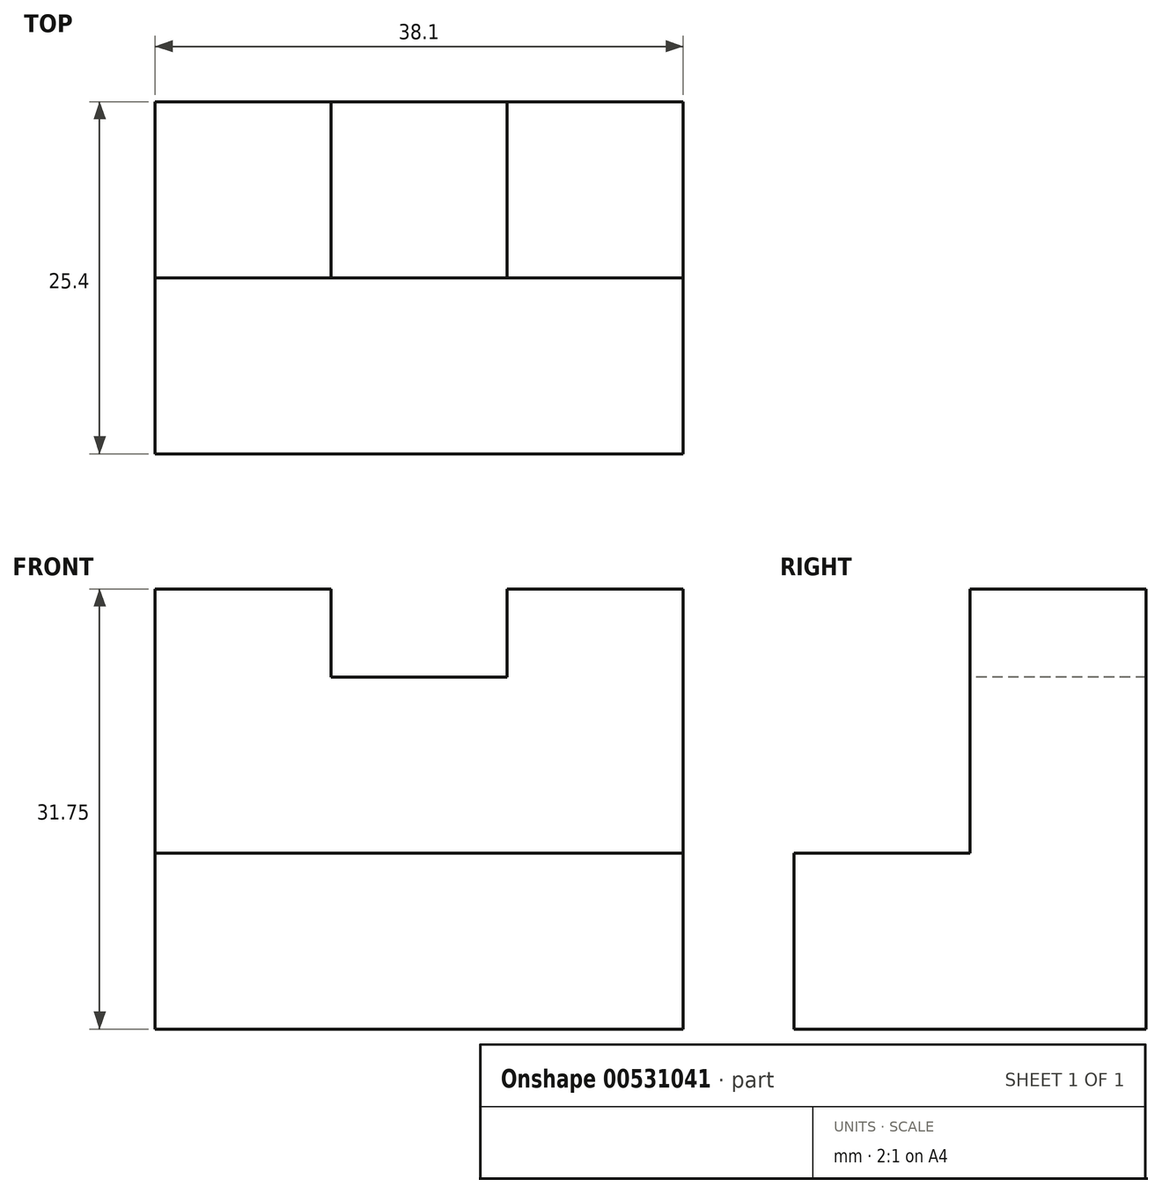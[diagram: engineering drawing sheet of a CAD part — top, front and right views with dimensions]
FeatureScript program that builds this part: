
annotation { "Feature Type Name" : "Feature", "Feature Type Description" : "" }
export const myFeature = defineFeature(function(context is Context, id is Id, definition is map)
    precondition{}
    {
        {
            var Q0;
            Q0=qCreatedBy(makeId("Right.planeOp"),FACE);
            var sketch = newSketch(context, id + "F0", { "sketchPlane" : qUnion([Q0])});
            skLineSegment(sketch, "E0", {"start": v(0, 0) * mm, "end": v(25.4, 0) * mm});
            skLineSegment(sketch, "E1", {"start": v(25.4, 0) * mm, "end": v(25.4, 31.75) * mm});
            skLineSegment(sketch, "E2", {"start": v(25.4, 31.75) * mm, "end": v(12.7, 31.75) * mm});
            skLineSegment(sketch, "E3", {"start": v(12.7, 31.75) * mm, "end": v(12.7, 12.7) * mm});
            skLineSegment(sketch, "E4", {"start": v(12.7, 12.7) * mm, "end": v(0, 12.7) * mm});
            skLineSegment(sketch, "E5", {"start": v(0, 12.7) * mm, "end": v(0, 0) * mm});
            skSolve(sketch);
        }
        {
            var Q0;
            Q0 = qSketchRegion(id + "F0", true);
            extrude(context, id + "F1", {"entities" : qUnion([Q0]), "depth" : 38.1 * mm, "offsetDistance" : 25.4 * mm});
        }
        {
            var Q0;
            Q0=makeQuery(id+"F1.opExtrude","SWEPT_FACE",FACE,{"disambiguationData":[OSD([sQuery(id+"F0.wireOp",EDGE,"E2")])]});
            var sketch = newSketch(context, id + "F2", { "sketchPlane" : qUnion([Q0])});
            skLineSegment(sketch, "E6", {"start": v(12.7, 25.4) * mm, "end": v(12.7, 12.7) * mm});
            skLineSegment(sketch, "E7", {"start": v(25.4, 25.4) * mm, "end": v(25.4, 12.7) * mm});
            skSolve(sketch);
        }
        {
            var Q0;
            Q0 = qSketchRegion(id + "F2", true);
            var Q1;
            {var subQ0=sQuery(id+"F2.wireOp",EDGE,"E6");Q1=makeQuery(id+"F2.imprint","IMPRINT",FACE,{"disambiguationData":[TD([[makeQuery(id+"F2.imprint","IMPRINT",EDGE,{"derivedFrom":subQ0}),1.0]])]});}
            extrude(context, id + "F3", {"entities" : qUnion([Q0, Q1]), "operationType" : NewBodyOperationType.REMOVE, "oppositeDirection" : true, "depth" : 6.35 * mm, "offsetDistance" : 25.4 * mm});
        }
    });
